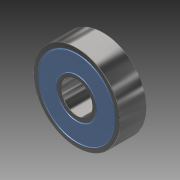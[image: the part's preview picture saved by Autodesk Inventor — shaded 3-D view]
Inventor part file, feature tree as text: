
AUTODESK INVENTOR PART (.ipt)
format: ipt  version: 2014 (Build 180170000, 170)  size: 178,688 bytes
history: native  units: in
note: dims shown in document units (in); Inventor stores cm internally (conversion verified against a paired STEP export)
features: sketch x2, extrude x1, fillet x1, revolve x1, plane x1, mirror x1
ambient origin geometry x8: Origin, YZ Plane, XZ Plane, XY Plane, X Axis, Y Axis, Z Axis, Center Point
bodies: Solid1 (feature_tree)
feature tree (7):
  extrude  "Extrusion1"  Depth=0.5118in
  fillet  "Fillet1"  Radius=0.5118in
  revolve  "Revolution1"  Angle=90.0deg
  plane  "Work Plane1"
  mirror  "Mirror1"
  sketch  "Sketch1"  dims[d0=0.5906in d1=1.6535in d2=0.5118in d3=0.0in]
  sketch  "Sketch2"  dims[d4=0.0118in d5=90.0deg]
